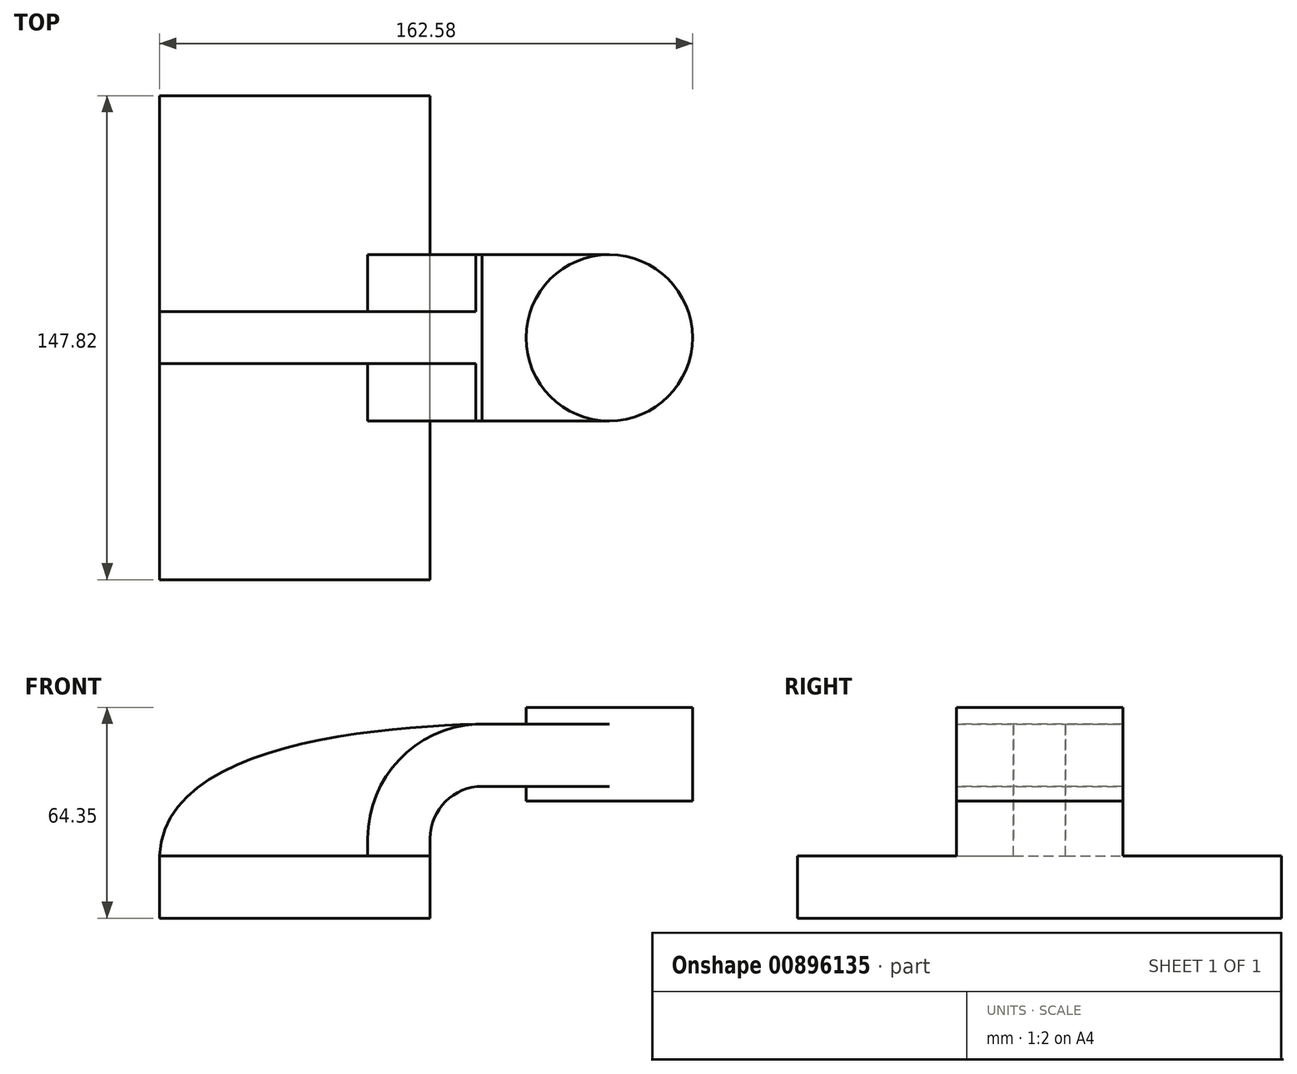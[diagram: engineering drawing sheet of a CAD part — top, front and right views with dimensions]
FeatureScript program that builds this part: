
annotation { "Feature Type Name" : "Feature", "Feature Type Description" : "" }
export const myFeature = defineFeature(function(context is Context, id is Id, definition is map)
    precondition{}
    {
        {
            var Q0;
            Q0=qCreatedBy(makeId("Front.planeOp"),FACE);
            var sketch = newSketch(context, id + "F0", { "sketchPlane" : qUnion([Q0])});
            skLineSegment(sketch, "E0.bottom", {"start": v(-41.28, -9.53) * mm, "end": v(41.28, -9.53) * mm});
            skLineSegment(sketch, "E0.top", {"start": v(-41.28, 9.53) * mm, "end": v(41.28, 9.53) * mm});
            skLineSegment(sketch, "E0.left", {"start": v(-41.28, -9.53) * mm, "end": v(-41.28, 9.53) * mm});
            skLineSegment(sketch, "E0.right", {"start": v(41.28, -9.53) * mm, "end": v(41.28, 9.53) * mm});
            skPoint(sketch, "E0.middle", {"position": v(0, 0) * mm});
            skLineSegment(sketch, "E1.bottom", {"start": v(121.3, 54.82) * mm, "end": v(70.5, 54.82) * mm});
            skLineSegment(sketch, "E1.top", {"start": v(121.3, 26.24) * mm, "end": v(70.5, 26.24) * mm});
            skLineSegment(sketch, "E1.left", {"start": v(121.3, 54.82) * mm, "end": v(121.3, 26.24) * mm});
            skLineSegment(sketch, "E1.right", {"start": v(70.5, 54.82) * mm, "end": v(70.5, 26.24) * mm});
            skPoint(sketch, "E1.middle", {"position": v(95.9, 40.53) * mm});
            skLineSegment(sketch, "E2", {"start": v(41.27, 9.53) * mm, "end": v(41.27, 14.86) * mm});
            skArc(sketch, "E3", {"start": v(41.27, 14.86) * mm, "mid": v(45.92, 26.09) * mm, "end": v(57.15, 30.74) * mm});
            skLineSegment(sketch, "E4", {"start": v(57.15, 30.74) * mm, "end": v(89.47, 30.74) * mm});
            skLineSegment(sketch, "E5.0", {"start": v(57.15, 49.79) * mm, "end": v(89.47, 49.79) * mm});
            skArc(sketch, "E5.1", {"start": v(22.23, 14.86) * mm, "mid": v(32.45, 39.56) * mm, "end": v(57.15, 49.79) * mm});
            skLineSegment(sketch, "E5.2", {"start": v(22.22, 9.53) * mm, "end": v(22.22, 14.86) * mm});
            skFitSpline(sketch, "E6", {"points": [v(-41.28, 9.52) * mm, v(57.15, 49.79) * mm], "startDerivative": vector(3.2, 101.1) * mm, "endDerivative": vector(103.06, 2.66) * mm});
            skPoint(sketch, "E7.orphan", {"position": v(95.9, 54.82) * mm});
            skPoint(sketch, "E8.end.orphan", {"position": v(95.9, 26.24) * mm});
            skLineSegment(sketch, "E9", {"start": v(95.9, 54.82) * mm, "end": v(95.9, 26.24) * mm});
            skLineSegment(sketch, "E10", {"start": v(89.47, 49.79) * mm, "end": v(95.9, 49.79) * mm});
            skLineSegment(sketch, "E11", {"start": v(89.47, 30.74) * mm, "end": v(95.9, 30.74) * mm});
            skSolve(sketch);
        }
        {
            var Q0;
            Q0=makeQuery(id+"F0.imprint","IMPRINT",FACE,{"disambiguationData":[TD([[makeQuery(id+"F0.imprint","IMPRINT",EDGE,{"derivedFrom":sQuery(id+"F0.wireOp",EDGE,"E0.bottom")}),1.0]])]});
            extrude(context, id + "F1", {"entities" : qUnion([Q0]), "depth" : 73.9 * mm, "offsetDistance" : 25.4 * mm, "hasSecondDirection" : true, "secondDirectionOppositeDirection" : true, "secondDirectionDepth" : 73.9 * mm});
        }
        {
            var Q0;
            {var subQ3=sQuery(id+"F0.wireOp",EDGE,"E5.2");Q0=makeQuery(id+"F0.imprint","IMPRINT",FACE,{"disambiguationData":[TD([[makeQuery(id+"F0.imprint","IMPRINT",EDGE,{"derivedFrom":subQ3}),1.0]])]});}
            extrude(context, id + "F2", {"entities" : qUnion([Q0]), "operationType" : NewBodyOperationType.ADD, "endBound" : BoundingType.SYMMETRIC, "depth" : 15.88 * mm, "offsetDistance" : 25.4 * mm});
        }
        {
            var Q0;
            {var subQ0=sQuery(id+"F0.wireOp",EDGE,"E10");Q0=makeQuery(id+"F0.imprint","IMPRINT",FACE,{"disambiguationData":[TD([[makeQuery(id+"F0.imprint","IMPRINT",EDGE,{"derivedFrom":subQ0}),-1.0]])]});}
            var Q1;
            {var subQ1=sQuery(id+"F0.wireOp",EDGE,"E2");Q1=makeQuery(id+"F0.imprint","IMPRINT",FACE,{"disambiguationData":[TD([[makeQuery(id+"F0.imprint","IMPRINT",EDGE,{"derivedFrom":subQ1}),1.0]])]});}
            extrude(context, id + "F3", {"entities" : qUnion([Q0, Q1]), "operationType" : NewBodyOperationType.ADD, "endBound" : BoundingType.SYMMETRIC, "depth" : 50.8 * mm, "offsetDistance" : 25.4 * mm});
        }
        {
            var Q0;
            {var subQ4=sQuery(id+"F0.wireOp",EDGE,"E1.left");Q0=makeQuery(id+"F0.imprint","IMPRINT",FACE,{"disambiguationData":[TD([[makeQuery(id+"F0.imprint","IMPRINT",EDGE,{"derivedFrom":subQ4}),-1.0]])]});}
            var Q1;
            Q1=sQuery(id+"F0.wireOp",EDGE,"E9");
            revolve(context, id + "F4", {"operationType" : NewBodyOperationType.ADD, "surfaceOperationType" : NewSurfaceOperationType.NEW, "entities" : qUnion([Q0]), "axis" : qUnion([Q1]), "revolveType" : RevolveType.FULL});
        }
    });
